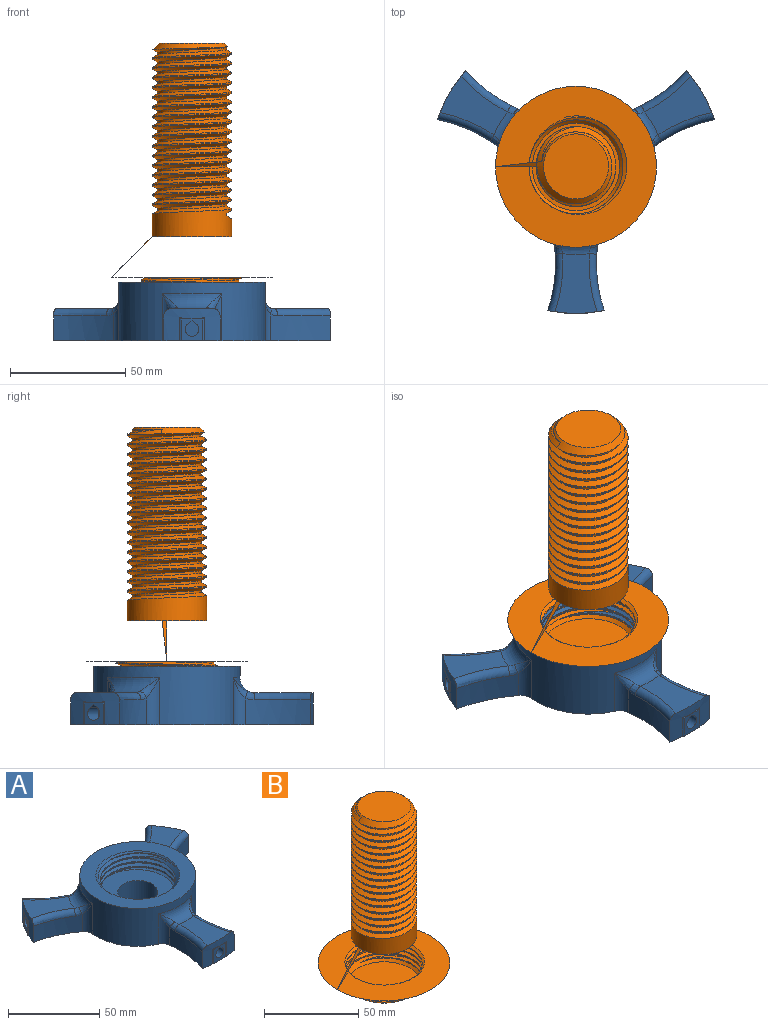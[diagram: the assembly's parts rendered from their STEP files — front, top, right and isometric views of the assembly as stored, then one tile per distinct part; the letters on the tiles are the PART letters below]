
ASSEMBLY  parts=2 mates=1
PART A: 107 faces, bbox 121.2x107.3x27 mm
  f0: plane 9.76x8.49mm, normal (0.87,0.5,0), area 61.2mm2, adj f17,f54,f55,f56,f68,f69,f74,f75
  f1: cylinder r=63.5mm len=21.19mm, axis (0,0,-1), area 232.4mm2, adj f10,f11,f13,f17,f68,f69,f74,f75
  f2: plane 9.76x8.49mm, normal (-0.87,0.5,0), area 61.2mm2, adj f17,f40,f41,f42,f70,f71,f76,f77
  f3: cylinder r=63.5mm len=21.19mm, axis (0,0,-1), area 232.4mm2, adj f8,f12,f14,f17,f70,f71,f76,f77
  f4: plane 9.76x9.76mm, normal (0,-1,0), area 61.2mm2, adj f17,f26,f27,f28,f72,f73,f78,f79
  f5: cylinder r=63.5mm len=24.47mm, axis (0,0,-1), area 232.4mm2, adj f9,f15,f16,f17,f72,f73,f78,f79
  f6: cylinder r=20.57mm len=41.14mm, axis (0,0,1), area 287.9mm2, adj f20,f21,f22,f23,f24
  f7: cylinder r=11mm len=22mm, axis (0,0,1), area 967.6mm2, adj f17,f20
  f8: cylinder r=63.5mm len=23.06mm, axis (0,0,-1), area 312.6mm2, adj f3,f17,f85,f104,f105
  f9: cylinder r=63.5mm len=28.32mm, axis (0,0,-1), area 312.6mm2, adj f5,f17,f88,f101,f102
  f10: cylinder r=63.5mm len=26mm, axis (0,0,-1), area 312.6mm2, adj f1,f17,f80,f98,f99
  f11: plane 29.23x25.44mm, normal (0,0,1), area 336.6mm2, adj f1,f81,f95,f98
  f12: plane 29.23x25.44mm, normal (0,0,1), area 336.6mm2, adj f3,f84,f92,f104
  f13: cylinder r=63.5mm len=23.06mm, axis (0,0,-1), area 312.6mm2, adj f1,f17,f82,f95,f96
  f14: cylinder r=63.5mm len=26mm, axis (0,0,-1), area 312.6mm2, adj f3,f17,f83,f92,f93
  f15: cylinder r=63.5mm len=28.32mm, axis (0,0,-1), area 312.6mm2, adj f5,f17,f86,f89,f90
  f16: plane 25.84x18.13mm, normal (0,0,1), area 336.6mm2, adj f5,f87,f89,f101
  f17: plane 120.16x105.25mm, normal (0,0,-1), area 4415.9mm2, adj f0,f1,f2,f3,f4,f5,f7,f8
  f18: cylinder r=31.75mm len=63.5mm, axis (0,0,1), area 3432.6mm2, adj f17,f19,f80,f81,f82,f83,f84,f85
  f19: plane 63.5x63.5mm, normal (0,0,1), area 1512.3mm2, adj f18,f21
  f20: plane 43.62x43.6mm, normal (0,0,1), area 1049.2mm2, adj f6,f7,f23,f24,f25
  f21: cone r=20.57mm half-angle=45deg, axis (0,0,1), area 300.8mm2, adj f6,f19,f22,f23,f24,f25
  f22: cone r=20.57mm half-angle=45deg, axis (0,0,1), area 17.7mm2, adj f6,f21,f24
  f23: bspline ~51.47x44.57mm, area 831.8mm2, adj f6,f20,f21,f25
  f24: bspline ~51.47x44.57mm, area 834.1mm2, adj f6,f20,f21,f22,f25
  f25: cylinder r=22.29mm len=44.57mm, axis (0,0,1), area 180.3mm2, adj f20,f21,f23,f24
  f26: plane 9x1.72mm, normal (0.57,0,-0.82), area 18.9mm2, adj f4,f27,f28,f35
  f27: cylinder r=3mm len=9mm, axis (0,-1,0), area 136.7mm2, adj f4,f26,f28,f35
  f28: plane 9x1.72mm, normal (-0.57,0,-0.82), area 18.9mm2, adj f4,f26,f27,f35
  f29: plane 6.35x5.55mm, normal (-0.87,0,-0.5), area 40.7mm2, adj f30,f33,f34,f35
  f30: plane 6.41x6.35mm, normal (0,0,-1), area 40.7mm2, adj f29,f31,f34,f35
  f31: plane 6.35x5.55mm, normal (0.87,0,-0.5), area 40.7mm2, adj f30,f32,f34,f35
  f32: plane 6.35x5mm, normal (1,0,0), area 31.8mm2, adj f17,f31,f34,f35
  f33: plane 6.35x5mm, normal (-1,0,0), area 31.8mm2, adj f17,f29,f34,f35
  f34: plane 12.82x10.55mm, normal (0,-1,0), area 88.4mm2, adj f17,f29,f30,f31,f32,f33,f37,f38
  f35: plane 12.82x10.55mm, normal (0,1,0), area 88.4mm2, adj f17,f26,f27,f28,f29,f30,f31,f32
  f36: plane 6.66x6mm, normal (0,-1,0), area 29.1mm2, adj f37,f38,f39
  f37: plane 9.65x1.72mm, normal (-0.57,0,-0.82), area 20.3mm2, adj f34,f36,f38,f39
  f38: cylinder r=3mm len=9.65mm, axis (0,-1,0), area 146.5mm2, adj f34,f36,f37,f39
  f39: plane 9.65x1.72mm, normal (0.57,0,-0.82), area 20.3mm2, adj f34,f36,f37,f38
  f40: plane 8.65x5.99mm, normal (-0.29,-0.5,-0.82), area 18.9mm2, adj f2,f41,f42,f49
  f41: cylinder r=3mm len=10.79mm, axis (-0.87,0.5,0), area 136.7mm2, adj f2,f40,f42,f49
  f42: plane 8.65x5.99mm, normal (0.29,0.5,-0.82), area 18.9mm2, adj f2,f40,f41,f49
  f43: plane 7.1x5.95mm, normal (0.43,0.75,-0.5), area 40.7mm2, adj f44,f47,f48,f49
  f44: plane 8.73x8.7mm, normal (0,0,-1), area 40.7mm2, adj f43,f45,f48,f49
  f45: plane 7.1x5.95mm, normal (-0.43,-0.75,-0.5), area 40.7mm2, adj f44,f46,f48,f49
  f46: plane 5.5x5mm, normal (-0.5,-0.87,0), area 31.7mm2, adj f17,f45,f48,f49
  f47: plane 5.5x5mm, normal (0.5,0.87,0), area 31.8mm2, adj f17,f43,f48,f49
  f48: plane 11.1x10.55mm, normal (-0.87,0.5,0), area 88.4mm2, adj f17,f43,f44,f45,f46,f47,f51,f52
  f49: plane 11.1x10.55mm, normal (0.87,-0.5,0), area 88.4mm2, adj f17,f40,f41,f42,f43,f44,f45,f46
  f50: plane 6.66x5.2mm, normal (-0.87,0.5,0), area 29.1mm2, adj f51,f52,f53
  f51: plane 9.22x6.32mm, normal (0.29,0.5,-0.82), area 20.3mm2, adj f48,f50,f52,f53
  f52: cylinder r=3mm len=11.36mm, axis (-0.87,0.5,0), area 146.5mm2, adj f48,f50,f51,f53
  f53: plane 9.22x6.32mm, normal (-0.29,-0.5,-0.82), area 20.3mm2, adj f48,f50,f51,f52
  f54: plane 8.65x5.99mm, normal (-0.29,0.5,-0.82), area 18.9mm2, adj f0,f55,f56,f63
  f55: cylinder r=3mm len=10.79mm, axis (0.87,0.5,0), area 136.7mm2, adj f0,f54,f56,f63
  f56: plane 8.65x5.99mm, normal (0.29,-0.5,-0.82), area 18.9mm2, adj f0,f54,f55,f63
  f57: plane 7.1x5.95mm, normal (0.43,-0.75,-0.5), area 40.7mm2, adj f58,f61,f62,f63
  f58: plane 8.73x8.7mm, normal (0,0,-1), area 40.7mm2, adj f57,f59,f62,f63
  f59: plane 7.1x5.95mm, normal (-0.43,0.75,-0.5), area 40.7mm2, adj f58,f60,f62,f63
  f60: plane 5.5x5mm, normal (-0.5,0.87,0), area 31.8mm2, adj f17,f59,f62,f63
  f61: plane 5.5x5mm, normal (0.5,-0.87,0), area 31.7mm2, adj f17,f57,f62,f63
  f62: plane 11.1x10.55mm, normal (0.87,0.5,0), area 88.4mm2, adj f17,f57,f58,f59,f60,f61,f65,f66
  f63: plane 11.1x10.55mm, normal (-0.87,-0.5,0), area 88.4mm2, adj f17,f54,f55,f56,f57,f58,f59,f60
  f64: plane 6.66x5.2mm, normal (0.87,0.5,0), area 29.1mm2, adj f65,f66,f67
  f65: plane 9.22x6.32mm, normal (0.29,-0.5,-0.82), area 20.3mm2, adj f62,f64,f66,f67
  f66: cylinder r=3mm len=11.36mm, axis (0.87,0.5,0), area 146.5mm2, adj f62,f64,f65,f67
  f67: plane 9.22x6.32mm, normal (-0.29,0.5,-0.82), area 20.3mm2, adj f62,f64,f65,f66
  f68: cylinder r=0.76mm len=10.03mm, axis (0,0,-1), area 5.2mm2, adj f0,f1,f17,f69
  f69: bspline ~5.2x3.22mm, area 0.9mm2, adj f0,f1,f68
  f70: cylinder r=0.76mm len=10.03mm, axis (0,0,-1), area 5.2mm2, adj f2,f3,f17,f71
  f71: bspline ~5.3x3mm, area 0.9mm2, adj f2,f3,f70
  f72: cylinder r=0.76mm len=10.03mm, axis (0,0,-1), area 5.2mm2, adj f4,f5,f17,f73
  f73: bspline ~6x0.59mm, area 1mm2, adj f4,f5,f72
  f74: cylinder r=0.76mm len=10.03mm, axis (0,0,-1), area 5.2mm2, adj f0,f1,f17,f75
  f75: bspline ~5.3x3mm, area 1mm2, adj f0,f1,f74
  f76: cylinder r=0.76mm len=10.03mm, axis (0,0,-1), area 5.2mm2, adj f2,f3,f17,f77
  f77: bspline ~5.2x3.22mm, area 1mm2, adj f2,f3,f76
  f78: cylinder r=0.76mm len=10.03mm, axis (0,0,-1), area 5.2mm2, adj f4,f5,f17,f79
  f79: bspline ~6x0.59mm, area 0.9mm2, adj f4,f5,f78
  f80: cylinder r=6.35mm len=20.35mm, axis (0,0,1), area 104.4mm2, adj f10,f17,f18,f100
  f81: torus R=38.1mm, axis (0,0,1), area 176.6mm2, adj f11,f18,f96,f97,f99,f100
  f82: cylinder r=6.35mm len=20.35mm, axis (0,0,-1), area 104.4mm2, adj f13,f17,f18,f97
  f83: cylinder r=6.35mm len=20.35mm, axis (0,0,-1), area 104.4mm2, adj f14,f17,f18,f94
  f84: torus R=38.1mm, axis (0,0,1), area 176.6mm2, adj f12,f18,f93,f94,f105,f106
  f85: cylinder r=6.35mm len=20.35mm, axis (0,0,1), area 104.4mm2, adj f8,f17,f18,f106
  f86: cylinder r=6.35mm len=20.35mm, axis (0,0,-1), area 104.4mm2, adj f15,f17,f18,f91
  f87: torus R=38.1mm, axis (0,0,1), area 176.6mm2, adj f16,f18,f90,f91,f102,f103
  f88: cylinder r=6.35mm len=20.35mm, axis (0,0,1), area 104.4mm2, adj f9,f17,f18,f103
  f89: torus R=66.67mm, axis (0,0,1), area 124.8mm2, adj f5,f15,f16,f90
  f90: bspline ~6.17x3.82mm, area 15.7mm2, adj f15,f87,f89,f91
  f91: bspline ~9.2x6.94mm, area 15.7mm2, adj f86,f87,f90
  f92: torus R=66.67mm, axis (0,0,1), area 124.8mm2, adj f3,f12,f14,f93
  f93: bspline ~6.39x6.08mm, area 15.7mm2, adj f14,f84,f92,f94
  f94: bspline ~9.35x9.2mm, area 15.7mm2, adj f83,f84,f93
  f95: torus R=66.67mm, axis (0,0,1), area 124.8mm2, adj f1,f11,f13,f96
  f96: bspline ~6.54x4.68mm, area 15.7mm2, adj f13,f81,f95,f97
  f97: bspline ~9.4x9.2mm, area 15.6mm2, adj f81,f82,f96
  f98: torus R=66.67mm, axis (0,0,1), area 124.8mm2, adj f1,f10,f11,f99
  f99: bspline ~6.39x6.08mm, area 15.7mm2, adj f10,f81,f98,f100
  f100: bspline ~8.88x8.83mm, area 15.7mm2, adj f80,f81,f99
  f101: torus R=66.67mm, axis (0,0,1), area 124.8mm2, adj f5,f9,f16,f102
  f102: bspline ~6.9x4.09mm, area 15.7mm2, adj f9,f87,f101,f103
  f103: bspline ~9.2x6.94mm, area 15.7mm2, adj f87,f88,f102
  f104: torus R=66.67mm, axis (0,0,1), area 124.8mm2, adj f3,f8,f12,f105
  f105: bspline ~6.54x4.68mm, area 15.7mm2, adj f8,f84,f104,f106
  f106: bspline ~9.4x9.2mm, area 15.6mm2, adj f84,f85,f105
PART B: 34 faces, bbox 70.8x70.8x116.1 mm
  f0: cylinder r=17.28mm len=34.56mm, axis (0,0,-1), area 46.9mm2, adj f1,f23,f25,f27
  f1: cylinder r=17.28mm len=34.56mm, axis (0,0,-1), area 57.5mm2, adj f0,f2,f25,f27
  f2: cylinder r=17.28mm len=34.56mm, axis (0,0,-1), area 57.6mm2, adj f1,f3,f25,f27
  f3: cylinder r=17.28mm len=34.56mm, axis (0,0,-1), area 57.5mm2, adj f2,f4,f25,f27
  f4: cylinder r=17.28mm len=34.56mm, axis (0,0,-1), area 57.4mm2, adj f3,f5,f25,f27
  f5: cylinder r=17.28mm len=34.56mm, axis (0,0,-1), area 57.4mm2, adj f4,f6,f25,f27
  f6: cylinder r=17.28mm len=34.56mm, axis (0,0,-1), area 57.4mm2, adj f5,f7,f25,f27
  f7: cylinder r=17.28mm len=34.56mm, axis (0,0,-1), area 57.4mm2, adj f6,f8,f25,f27
  f8: cylinder r=17.28mm len=34.56mm, axis (0,0,-1), area 57.3mm2, adj f7,f9,f25,f27
  f9: cylinder r=17.28mm len=34.56mm, axis (0,0,-1), area 57.3mm2, adj f8,f10,f25,f27
  f10: cylinder r=17.28mm len=34.56mm, axis (0,0,-1), area 57.5mm2, adj f9,f11,f25,f27
  f11: cylinder r=17.28mm len=34.56mm, axis (0,0,-1), area 57.6mm2, adj f10,f12,f25,f27
  f12: cylinder r=17.28mm len=34.56mm, axis (0,0,-1), area 57.6mm2, adj f11,f13,f25,f27
  f13: cylinder r=17.28mm len=34.56mm, axis (0,0,-1), area 57.4mm2, adj f12,f14,f25,f27
  f14: cylinder r=17.28mm len=34.56mm, axis (0,0,-1), area 57.2mm2, adj f13,f15,f25,f27
  f15: cylinder r=17.28mm len=34.56mm, axis (0,0,-1), area 57.3mm2, adj f14,f16,f25,f27
  f16: cylinder r=17.28mm len=34.56mm, axis (0,0,-1), area 1075mm2, adj f15,f17,f25,f27,f28,f29,f30
  f17: cone r=34.92mm half-angle=45deg, axis (0,0,-1), area 4092.7mm2, adj f16,f20
  f18: plane 37.85x37.85mm, normal (0,0,-1), area 1125.2mm2, adj f22
  f19: cylinder r=22.1mm len=44.2mm, axis (0,0,1), area 165.6mm2, adj f20,f22,f31,f33
  f20: plane 70.78x70.78mm, normal (0,0,-1), area 2427.5mm2, adj f17,f19,f31,f32,f33
  f21: plane 28.21x28.21mm, normal (0,0,1), area 624.9mm2, adj f24
  f22: cone r=22.1mm half-angle=45deg, axis (0,0,1), area 394.8mm2, adj f18,f19,f31,f32,f33
  f23: cone r=17.28mm half-angle=45deg, axis (0,0,-1), area 36.1mm2, adj f0,f24,f25,f27
  f24: cone r=17.28mm half-angle=45deg, axis (0,0,-1), area 219.6mm2, adj f21,f23,f25,f26
  f25: bspline ~74.7x39.9mm, area 4507.2mm2, adj f0,f1,f2,f3,f4,f5,f6,f7
  f26: cylinder r=14.99mm len=73.99mm, axis (0,0,-1), area 1627.8mm2, adj f24,f25,f27,f30
  f27: bspline ~75.41x39.9mm, area 4659.4mm2, adj f0,f1,f2,f3,f4,f5,f6,f7
  f28: plane 8.6x2.29mm, normal (0.5,0,0.87), area 15.4mm2, adj f16,f27,f30
  f29: plane 8.6x2.29mm, normal (0.5,0,-0.87), area 15.4mm2, adj f16,f25,f30
  f30: plane 8.6x1.06mm, normal (1,0,0), area 9.1mm2, adj f16,f26,f28,f29
  f31: bspline ~51.04x44.2mm, area 865.8mm2, adj f19,f20,f22,f32
  f32: cylinder r=20.38mm len=40.76mm, axis (0,0,1), area 360.3mm2, adj f20,f22,f31,f33
  f33: bspline ~51.04x44.2mm, area 865mm2, adj f19,f20,f22,f32
PLACE A t=(85.43,49.68,0)mm
PLACE B t=(85.43,49.68,14.86)mm
MATE cylindrical B.f0 <-> A.f18  axis (0,0,-1) through (85.43,49.68,36.38)mm
